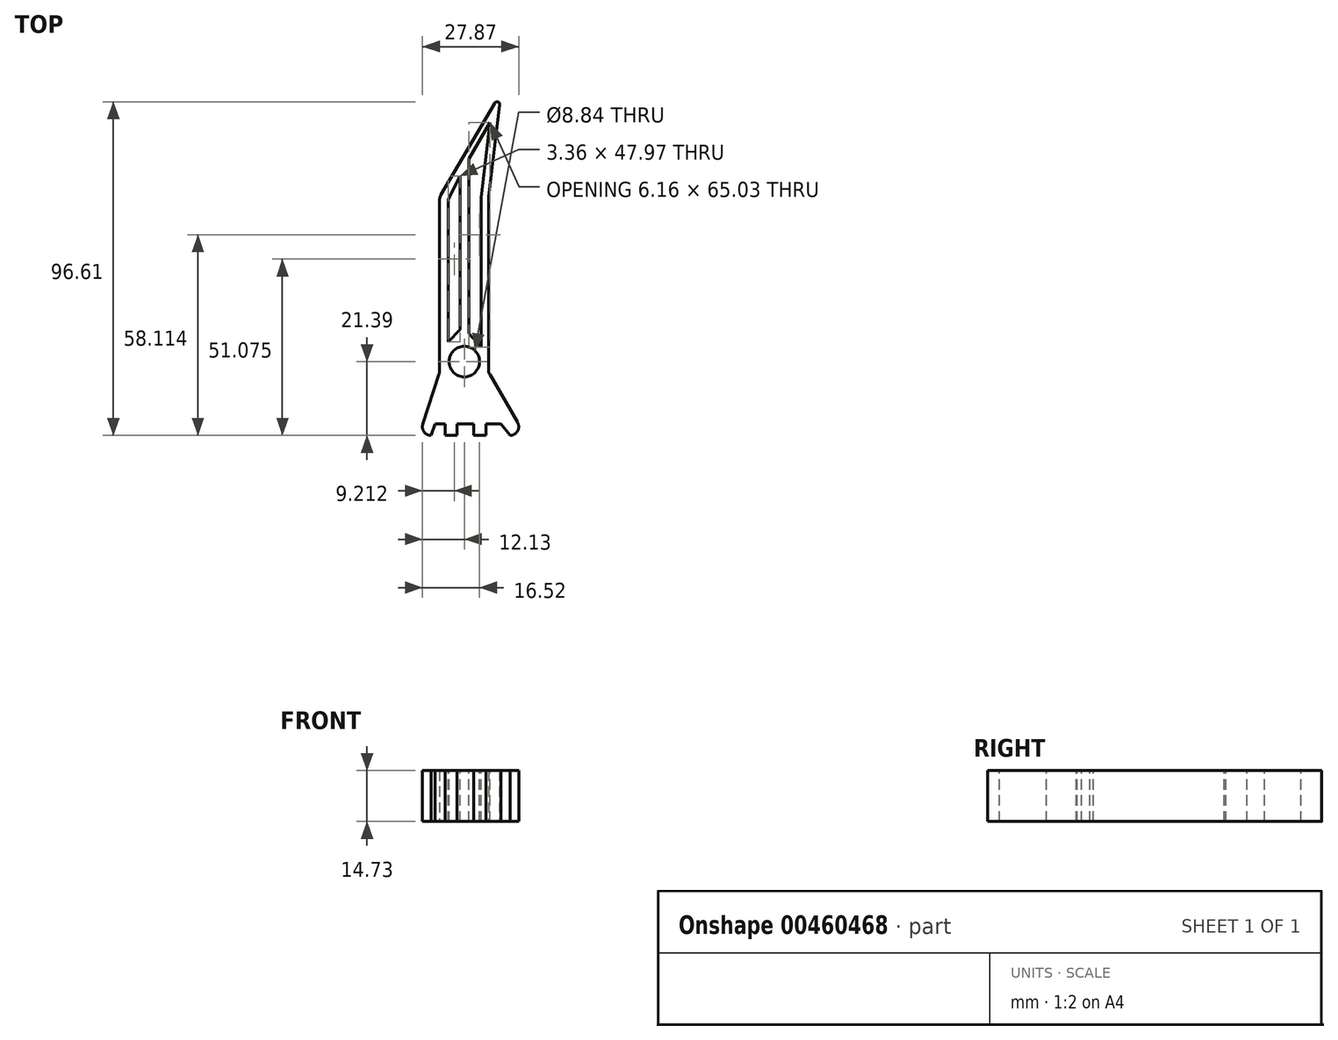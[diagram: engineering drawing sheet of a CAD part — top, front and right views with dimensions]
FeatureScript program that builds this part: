
annotation { "Feature Type Name" : "Feature", "Feature Type Description" : "" }
export const myFeature = defineFeature(function(context is Context, id is Id, definition is map)
    precondition{}
    {
        {
            var Q0;
            Q0=qCreatedBy(makeId("Top.planeOp"),FACE);
            var sketch = newSketch(context, id + "F0", { "sketchPlane" : qUnion([Q0])});
            skLineSegment(sketch, "E0.bottom", {"start": v(-7.14, 22.88) * mm, "end": v(7, 22.88) * mm});
            skLineSegment(sketch, "E0.top", {"start": v(-7.14, -27.92) * mm, "end": v(7, -27.92) * mm});
            skLineSegment(sketch, "E0.left", {"start": v(-7.14, 22.88) * mm, "end": v(-7.14, -27.92) * mm});
            skLineSegment(sketch, "E0.right", {"start": v(7, 22.88) * mm, "end": v(7, -27.92) * mm});
            skLineSegment(sketch, "E1", {"start": v(-7.14, 22.88) * mm, "end": v(10.73, 53.36) * mm});
            skLineSegment(sketch, "E2", {"start": v(10.73, 53.36) * mm, "end": v(7, 22.88) * mm});
            skLineSegment(sketch, "E3", {"start": v(-7.14, -27.92) * mm, "end": v(-13.1, -46.16) * mm});
            skLineSegment(sketch, "E4", {"start": v(-13.1, -46.16) * mm, "end": v(17.61, -46.16) * mm});
            skLineSegment(sketch, "E5", {"start": v(17.61, -46.16) * mm, "end": v(7, -27.92) * mm});
            skSolve(sketch);
        }
        {
            var Q0;
            Q0 = qSketchRegion(id + "F0", true);
            var Q1;
            Q1=makeQuery(id+"F0.imprint","IMPRINT",FACE,{"disambiguationData":[TD([[makeQuery(id+"F0.imprint","IMPRINT",EDGE,{"derivedFrom":sQuery(id+"F0.wireOp",EDGE,"E0.top")}),-1.0]])]});
            extrude(context, id + "F1", {"entities" : qUnion([Q0, Q1]), "depth" : 14.73 * mm});
        }
        {
            var Q0;
            Q0=makeQuery(id+"F1.opExtrude","SWEPT_EDGE",EDGE,{"disambiguationData":[OSD([sQuery(id+"F0.wireOp",EDGE,"E0.top"),sQuery(id+"F0.wireOp",EDGE,"E0.right"),sQuery(id+"F0.wireOp",EDGE,"E5")])]});
            var Q1;
            Q1=makeQuery(id+"F1.opExtrude","SWEPT_EDGE",EDGE,{"disambiguationData":[OSD([sQuery(id+"F0.wireOp",EDGE,"E0.bottom"),sQuery(id+"F0.wireOp",EDGE,"E0.right"),sQuery(id+"F0.wireOp",EDGE,"E2")])]});
            var Q2;
            Q2=makeQuery(id+"F1.opExtrude","SWEPT_EDGE",EDGE,{"disambiguationData":[OSD([sQuery(id+"F0.wireOp",EDGE,"E3"),sQuery(id+"F0.wireOp",EDGE,"E4")])]});
            var Q3;
            Q3=makeQuery(id+"F1.opExtrude","SWEPT_EDGE",EDGE,{"disambiguationData":[OSD([sQuery(id+"F0.wireOp",EDGE,"E4"),sQuery(id+"F0.wireOp",EDGE,"E5")])]});
            var Q4;
            Q4=makeQuery(id+"F1.opExtrude","SWEPT_EDGE",EDGE,{"disambiguationData":[OSD([sQuery(id+"F0.wireOp",EDGE,"E0.bottom"),sQuery(id+"F0.wireOp",EDGE,"E0.left"),sQuery(id+"F0.wireOp",EDGE,"E1")])]});
            var Q5;
            Q5=makeQuery(id+"F1.opExtrude","SWEPT_EDGE",EDGE,{"disambiguationData":[OSD([sQuery(id+"F0.wireOp",EDGE,"E0.top"),sQuery(id+"F0.wireOp",EDGE,"E0.left"),sQuery(id+"F0.wireOp",EDGE,"E3")])]});
            fillet(context, id + "F2", {"entities" : qUnion([Q0, Q1, Q2, Q3, Q4, Q5]), "radius" : 2.54 * mm, "tangentPropagation" : true, "allowEdgeOverflow" : false});
        }
        {
            var Q0;
            Q0=makeQuery(id+"F1.opExtrude","SWEPT_EDGE",EDGE,{"disambiguationData":[OSD([sQuery(id+"F0.wireOp",EDGE,"E1"),sQuery(id+"F0.wireOp",EDGE,"E2")])]});
            fillet(context, id + "F3", {"entities" : qUnion([Q0]), "radius" : 0.8 * mm, "tangentPropagation" : true, "allowEdgeOverflow" : false});
        }
        {
            var Q0;
            Q0=makeQuery(id+"F1.opExtrude","CAP_FACE",FACE,{"disambiguationData":[OSD([sQuery(id+"F0.wireOp",EDGE,"E0.left"),sQuery(id+"F0.wireOp",EDGE,"E0.right"),sQuery(id+"F0.wireOp",EDGE,"E1"),sQuery(id+"F0.wireOp",EDGE,"E2"),sQuery(id+"F0.wireOp",EDGE,"E3"),sQuery(id+"F0.wireOp",EDGE,"E4"),sQuery(id+"F0.wireOp",EDGE,"E5")])],"isStart":false});
            var sketch = newSketch(context, id + "F4", { "sketchPlane" : qUnion([Q0])});
            skLineSegment(sketch, "E6", {"start": v(0, 35.06) * mm, "end": v(0, -46.16) * mm, "construction": true});
            skCircle(sketch, "E7", {"center": v(0, -24.77) * mm, "radius": 4.42 * mm});
            skLineSegment(sketch, "E8", {"start": v(-4.6, 22.2) * mm, "end": v(-4.6, -19.07) * mm});
            skLineSegment(sketch, "E9", {"start": v(-4.6, -19.07) * mm, "end": v(-1.24, -15.53) * mm});
            skLineSegment(sketch, "E10", {"start": v(-1.24, -15.53) * mm, "end": v(-1.24, 28.9) * mm});
            skLineSegment(sketch, "E11", {"start": v(-1.24, 28.9) * mm, "end": v(-4.6, 22.2) * mm});
            skLineSegment(sketch, "E12", {"start": v(1.31, 28.55) * mm, "end": v(1.31, -16.67) * mm});
            skLineSegment(sketch, "E13", {"start": v(1.31, -16.67) * mm, "end": v(4.81, -20.56) * mm});
            skLineSegment(sketch, "E14", {"start": v(4.81, -20.56) * mm, "end": v(4.81, 22.73) * mm});
            skLineSegment(sketch, "E15", {"start": v(4.81, 22.73) * mm, "end": v(7.47, 44.47) * mm});
            skLineSegment(sketch, "E16", {"start": v(7.47, 44.47) * mm, "end": v(1.31, 33.96) * mm});
            skLineSegment(sketch, "E17", {"start": v(1.31, 33.96) * mm, "end": v(1.31, 28.55) * mm});
            skLineSegment(sketch, "E18", {"start": v(-9.59, -46.16) * mm, "end": v(-8.5, -42.83) * mm});
            skLineSegment(sketch, "E19", {"start": v(-8.5, -42.83) * mm, "end": v(-5.5, -42.83) * mm});
            skLineSegment(sketch, "E20", {"start": v(-5.5, -42.83) * mm, "end": v(-5.5, -46.16) * mm});
            skLineSegment(sketch, "E21", {"start": v(-5.5, -46.16) * mm, "end": v(-9.59, -46.16) * mm});
            skLineSegment(sketch, "E22", {"start": v(-2.16, -46.16) * mm, "end": v(-2.16, -42.83) * mm});
            skLineSegment(sketch, "E23", {"start": v(-2.16, -42.83) * mm, "end": v(2.75, -42.83) * mm});
            skLineSegment(sketch, "E24", {"start": v(2.75, -42.83) * mm, "end": v(2.75, -46.16) * mm});
            skLineSegment(sketch, "E25", {"start": v(2.75, -46.16) * mm, "end": v(-2.16, -46.16) * mm});
            skLineSegment(sketch, "E26", {"start": v(6.3, -46.16) * mm, "end": v(6.3, -42.83) * mm});
            skLineSegment(sketch, "E27", {"start": v(6.3, -42.83) * mm, "end": v(10.62, -42.83) * mm});
            skLineSegment(sketch, "E28", {"start": v(10.62, -42.83) * mm, "end": v(13.2, -46.16) * mm});
            skLineSegment(sketch, "E29", {"start": v(13.2, -46.16) * mm, "end": v(6.3, -46.16) * mm});
            skSolve(sketch);
        }
        {
            var Q0;
            Q0 = qSketchRegion(id + "F4", true);
            extrude(context, id + "F5", {"entities" : qUnion([Q0]), "operationType" : NewBodyOperationType.REMOVE, "oppositeDirection" : true, "depth" : 38.1 * mm});
        }
    });
